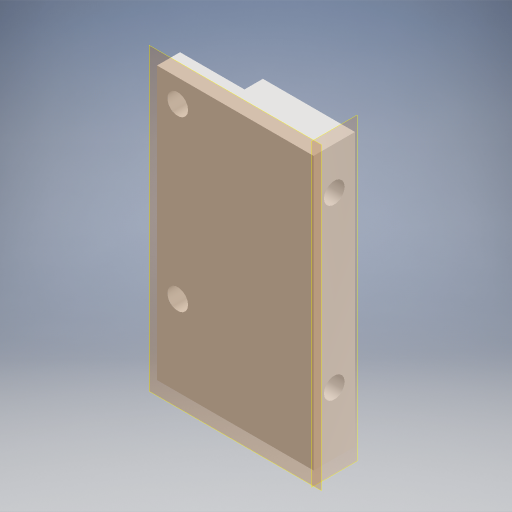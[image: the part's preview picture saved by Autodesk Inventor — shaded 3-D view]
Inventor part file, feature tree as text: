
AUTODESK INVENTOR PART (.ipt)
format: ipt  version: 2024 (Build 280153000, 153)  size: 275,456 bytes
history: native  units: in
note: dims shown in document units (in); Inventor stores cm internally (conversion verified against a paired STEP export)
features: other x5, extrude x3, sketch x3, reference x3
ambient origin geometry x8: Origin, YZ Plane, XZ Plane, XY Plane, X Axis, Y Axis, Z Axis, Center Point
bodies: Body1 (feature_tree)
feature tree (14):
  other  "솔리드1"
  other  "작업 평면1"
  extrude  "돌출1"  Depth=0.1181in TaperAngle=0.0deg
  other  "작업 평면2"
  extrude  "돌출2"  Depth=0.4724in TaperAngle=0.0deg
  extrude  "돌출3"  Depth=0.4724in TaperAngle=0.0deg
  sketch  "스케치1"
  reference  "참조1"
  sketch  "스케치2"
  reference  "참조2"
  sketch  "스케치3"
  reference  "참조3"
  other  "조립품9"
  other  "foot_right_connection_MIR:1"
